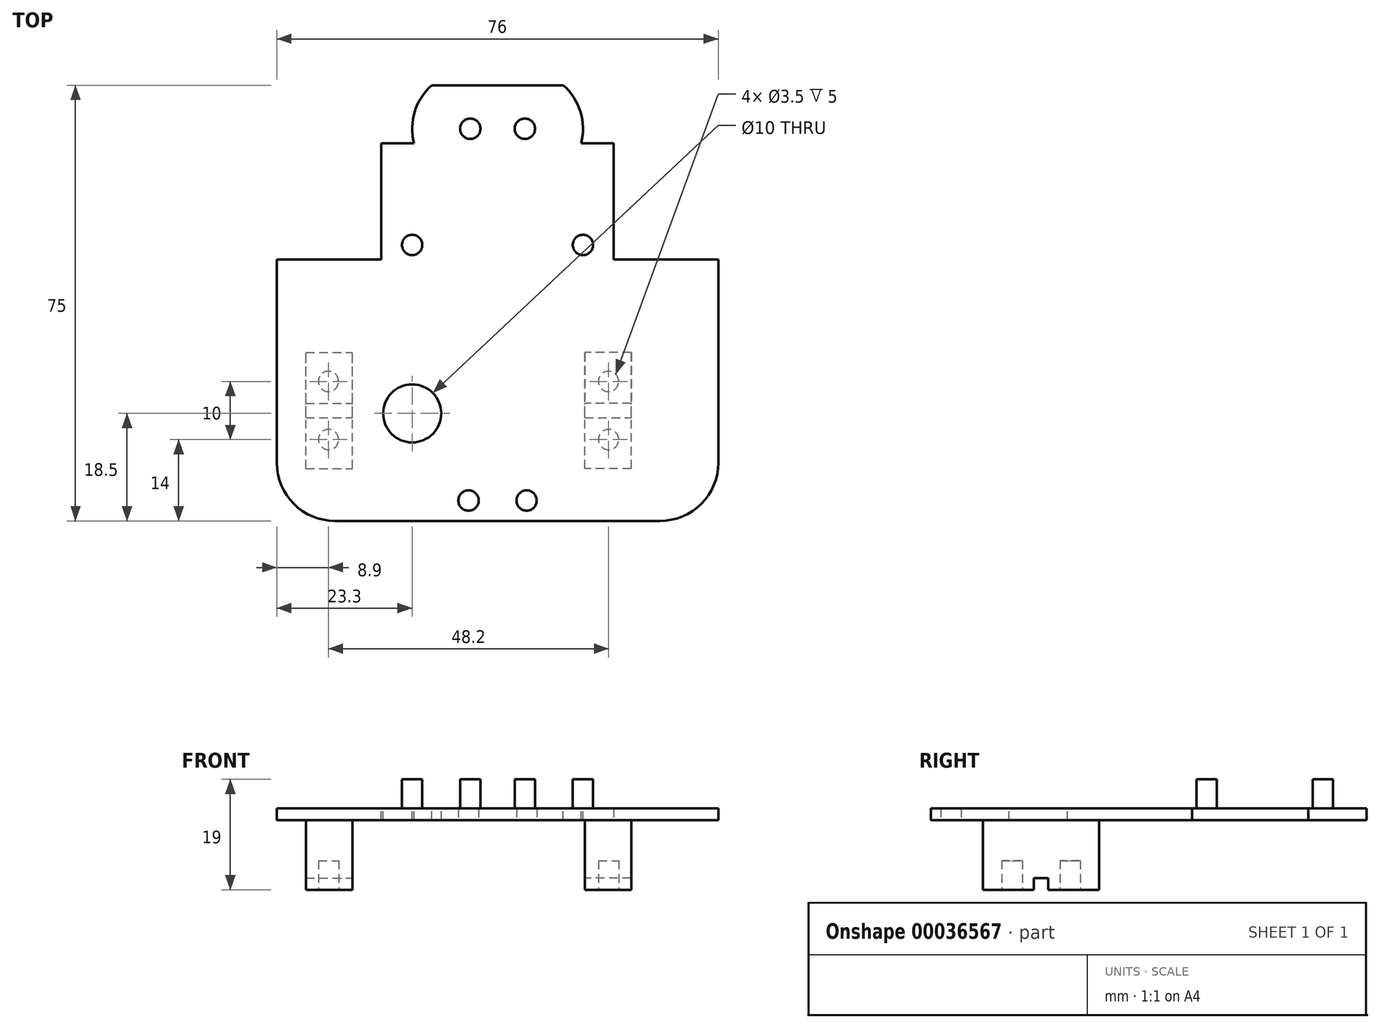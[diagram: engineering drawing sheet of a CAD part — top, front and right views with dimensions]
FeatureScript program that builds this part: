
annotation { "Feature Type Name" : "Feature", "Feature Type Description" : "" }
export const myFeature = defineFeature(function(context is Context, id is Id, definition is map)
    precondition{}
    {
        {
            var Q0;
            Q0=qCreatedBy(makeId("Top.planeOp"),FACE);
            var sketch = newSketch(context, id + "F0", { "sketchPlane" : qUnion([Q0])});
            skLineSegment(sketch, "E0.bottom", {"start": v(-20, 27.5) * mm, "end": v(20, 27.5) * mm});
            skLineSegment(sketch, "E0.top", {"start": v(-20, -2.5) * mm, "end": v(20, -2.5) * mm});
            skLineSegment(sketch, "E0.left", {"start": v(-20, 27.5) * mm, "end": v(-20, -2.5) * mm});
            skLineSegment(sketch, "E0.right", {"start": v(20, 27.5) * mm, "end": v(20, -2.5) * mm});
            skSolve(sketch);
        }
        {
            var Q0;
            Q0 = qSketchRegion(id + "F0", true);
            extrude(context, id + "F1", {"entities" : qUnion([Q0]), "depth" : 2 * mm});
        }
        {
            var Q0;
            Q0=makeQuery(id+"F1.opExtrude","CAP_FACE",FACE,{"disambiguationData":[OSD([sQuery(id+"F0.wireOp",EDGE,"E0.bottom"),sQuery(id+"F0.wireOp",EDGE,"E0.top"),sQuery(id+"F0.wireOp",EDGE,"E0.left"),sQuery(id+"F0.wireOp",EDGE,"E0.right")])],"isStart":false});
            var sketch = newSketch(context, id + "F2", { "sketchPlane" : qUnion([Q0])});
            skCircle(sketch, "E1", {"center": v(14.7, 0) * mm, "radius": 1.75 * mm});
            skCircle(sketch, "E2", {"center": v(-14.7, 0) * mm, "radius": 1.75 * mm});
            skSolve(sketch);
        }
        {
            var Q0;
            Q0=makeQuery(id+"F2.imprint","IMPRINT",FACE,{"disambiguationData":[TD([[makeQuery(id+"F2.imprint","IMPRINT",EDGE,{"derivedFrom":sQuery(id+"F2.wireOp",EDGE,"E1")}),1.0]])]});
            var Q1;
            Q1=makeQuery(id+"F2.imprint","IMPRINT",FACE,{"disambiguationData":[TD([[makeQuery(id+"F2.imprint","IMPRINT",EDGE,{"derivedFrom":sQuery(id+"F2.wireOp",EDGE,"E2")}),1.0]])]});
            extrude(context, id + "F3", {"entities" : qUnion([Q0, Q1]), "operationType" : NewBodyOperationType.ADD, "depth" : 5 * mm});
        }
        {
            var Q0;
            Q0=makeQuery(id+"F1.opExtrude","CAP_FACE",FACE,{"disambiguationData":[OSD([sQuery(id+"F0.wireOp",EDGE,"E0.bottom"),sQuery(id+"F0.wireOp",EDGE,"E0.top"),sQuery(id+"F0.wireOp",EDGE,"E0.left"),sQuery(id+"F0.wireOp",EDGE,"E0.right")])],"isStart":false});
            var sketch = newSketch(context, id + "F4", { "sketchPlane" : qUnion([Q0])});
            skCircle(sketch, "E3", {"center": v(-4.7, 20) * mm, "radius": 1.75 * mm});
            skCircle(sketch, "E4", {"center": v(4.7, 20) * mm, "radius": 1.75 * mm});
            skSolve(sketch);
        }
        {
            var Q0;
            Q0=makeQuery(id+"F4.imprint","IMPRINT",FACE,{"disambiguationData":[TD([[makeQuery(id+"F4.imprint","IMPRINT",EDGE,{"derivedFrom":sQuery(id+"F4.wireOp",EDGE,"E3")}),1.0]])]});
            var Q1;
            Q1=makeQuery(id+"F4.imprint","IMPRINT",FACE,{"disambiguationData":[TD([[makeQuery(id+"F4.imprint","IMPRINT",EDGE,{"derivedFrom":sQuery(id+"F4.wireOp",EDGE,"E4")}),1.0]])]});
            extrude(context, id + "F5", {"entities" : qUnion([Q0, Q1]), "operationType" : NewBodyOperationType.ADD, "depth" : 5 * mm});
        }
        {
            var Q0;
            Q0=makeQuery(id+"F2.imprint","IMPRINT",FACE,{"disambiguationData":[TD([[makeQuery(id+"F2.imprint","IMPRINT",EDGE,{"derivedFrom":sQuery(id+"F2.wireOp",EDGE,"E1")}),-1.0]])]});
            var sketch = newSketch(context, id + "F6", { "sketchPlane" : qUnion([Q0])});
            skArc(sketch, "E5", {"start": v(-11.3, 27.51) * mm, "mid": v(-14.26, 22.94) * mm, "end": v(-14.38, 17.5) * mm});
            skLineSegment(sketch, "E6", {"start": v(-20, 17.5) * mm, "end": v(-14.38, 17.5) * mm});
            skLineSegment(sketch, "E7", {"start": v(-20, 17.5) * mm, "end": v(-20, 27.51) * mm});
            skLineSegment(sketch, "E8", {"start": v(-20, 27.51) * mm, "end": v(-11.3, 27.51) * mm});
            skLineSegment(sketch, "E9", {"start": v(0, 31.6) * mm, "end": v(0, 7.91) * mm, "construction": true});
            skArc(sketch, "E10.MirrorCS", {"start": v(11.3, 27.51) * mm, "mid": v(14.26, 22.94) * mm, "end": v(14.38, 17.5) * mm});
            skLineSegment(sketch, "E11.MirrorCS", {"start": v(20, 27.51) * mm, "end": v(11.3, 27.51) * mm});
            skLineSegment(sketch, "E12.MirrorCS", {"start": v(20, 17.5) * mm, "end": v(20, 27.51) * mm});
            skLineSegment(sketch, "E13.MirrorCS", {"start": v(20, 17.5) * mm, "end": v(14.38, 17.5) * mm});
            skSolve(sketch);
        }
        {
            var Q0;
            Q0 = qSketchRegion(id + "F6", true);
            extrude(context, id + "F7", {"entities" : qUnion([Q0]), "operationType" : NewBodyOperationType.REMOVE, "endBound" : BoundingType.THROUGH_ALL, "oppositeDirection" : true, "depth" : 25 * mm});
        }
        {
            var Q0;
            Q0=qCreatedBy(makeId("Top.planeOp"),FACE);
            var sketch = newSketch(context, id + "F8", { "sketchPlane" : qUnion([Q0])});
            skLineSegment(sketch, "E14.bottom", {"start": v(-50, -2.5) * mm, "end": v(50, -2.5) * mm});
            skLineSegment(sketch, "E14.top", {"start": v(-50, -52.5) * mm, "end": v(50, -52.5) * mm});
            skLineSegment(sketch, "E14.left", {"start": v(-50, -2.5) * mm, "end": v(-50, -52.5) * mm});
            skLineSegment(sketch, "E14.right", {"start": v(50, -2.5) * mm, "end": v(50, -52.5) * mm});
            skSolve(sketch);
        }
        {
            var Q0;
            Q0 = qSketchRegion(id + "F8", true);
            extrude(context, id + "F9", {"entities" : qUnion([Q0]), "operationType" : NewBodyOperationType.ADD, "depth" : 2 * mm});
        }
        {
            var Q0;
            Q0=makeQuery(id+"F9.boolean.opBoolean","MERGE",FACE,{"derivedFrom":[makeQuery(id+"F1.opExtrude","CAP_FACE",FACE,{"disambiguationData":[OSD([sQuery(id+"F0.wireOp",EDGE,"E0.bottom"),sQuery(id+"F0.wireOp",EDGE,"E0.top"),sQuery(id+"F0.wireOp",EDGE,"E0.left"),sQuery(id+"F0.wireOp",EDGE,"E0.right")])],"isStart":false}),makeQuery(id+"F9.opExtrude","CAP_FACE",FACE,{"disambiguationData":[OSD([sQuery(id+"F8.wireOp",EDGE,"E14.bottom"),sQuery(id+"F8.wireOp",EDGE,"E14.top"),sQuery(id+"F8.wireOp",EDGE,"E14.left"),sQuery(id+"F8.wireOp",EDGE,"E14.right")])],"isStart":false})]});
            var sketch = newSketch(context, id + "F10", { "sketchPlane" : qUnion([Q0])});
            skCircle(sketch, "E15", {"center": v(-14.7, -29) * mm, "radius": 5 * mm});
            skSolve(sketch);
        }
        {
            var Q0;
            Q0 = qSketchRegion(id + "F10", true);
            extrude(context, id + "F11", {"entities" : qUnion([Q0]), "operationType" : NewBodyOperationType.REMOVE, "endBound" : BoundingType.THROUGH_ALL, "oppositeDirection" : true, "depth" : 25 * mm});
        }
        {
            var Q0;
            Q0=makeQuery(id+"F9.boolean.opBoolean","MERGE",FACE,{"derivedFrom":[makeQuery(id+"F1.opExtrude","CAP_FACE",FACE,{"disambiguationData":[OSD([sQuery(id+"F0.wireOp",EDGE,"E0.bottom"),sQuery(id+"F0.wireOp",EDGE,"E0.top"),sQuery(id+"F0.wireOp",EDGE,"E0.left"),sQuery(id+"F0.wireOp",EDGE,"E0.right")])],"isStart":true}),makeQuery(id+"F9.opExtrude","CAP_FACE",FACE,{"disambiguationData":[OSD([sQuery(id+"F8.wireOp",EDGE,"E14.bottom"),sQuery(id+"F8.wireOp",EDGE,"E14.top"),sQuery(id+"F8.wireOp",EDGE,"E14.left"),sQuery(id+"F8.wireOp",EDGE,"E14.right")])],"isStart":true})]});
            var sketch = newSketch(context, id + "F12", { "sketchPlane" : qUnion([Q0])});
            skLineSegment(sketch, "E16.bottom", {"start": v(-33, 38.5) * mm, "end": v(-25, 38.5) * mm});
            skLineSegment(sketch, "E16.top", {"start": v(-33, 18.5) * mm, "end": v(-25, 18.5) * mm});
            skLineSegment(sketch, "E16.left", {"start": v(-33, 38.5) * mm, "end": v(-33, 18.5) * mm});
            skLineSegment(sketch, "E16.right", {"start": v(-25, 38.5) * mm, "end": v(-25, 18.5) * mm});
            skLineSegment(sketch, "E17", {"start": v(-5, 39.4) * mm, "end": v(-5, 13.63) * mm, "construction": true});
            skLineSegment(sketch, "E18.MirrorCS", {"start": v(15, 38.5) * mm, "end": v(15, 18.5) * mm});
            skLineSegment(sketch, "E19.MirrorCS", {"start": v(23, 38.5) * mm, "end": v(15, 38.5) * mm});
            skLineSegment(sketch, "E20.MirrorCS", {"start": v(23, 38.5) * mm, "end": v(23, 18.5) * mm});
            skLineSegment(sketch, "E21.MirrorCS", {"start": v(23, 18.5) * mm, "end": v(15, 18.5) * mm});
            skSolve(sketch);
        }
        {
            var Q0;
            Q0 = qSketchRegion(id + "F12", true);
            extrude(context, id + "F13", {"entities" : qUnion([Q0]), "operationType" : NewBodyOperationType.ADD, "depth" : 10 * mm});
        }
        {
            var Q0;
            Q0=makeQuery(id+"F13.opExtrude","CAP_FACE",FACE,{"disambiguationData":[OSD([sQuery(id+"F12.wireOp",EDGE,"E16.bottom"),sQuery(id+"F12.wireOp",EDGE,"E16.top"),sQuery(id+"F12.wireOp",EDGE,"E16.left"),sQuery(id+"F12.wireOp",EDGE,"E16.right")])],"isStart":false});
            var sketch = newSketch(context, id + "F14", { "sketchPlane" : qUnion([Q0])});
            skLineSegment(sketch, "E22.bottom", {"start": v(-33, 18.5) * mm, "end": v(-25, 18.5) * mm});
            skLineSegment(sketch, "E22.top", {"start": v(-33, 27.25) * mm, "end": v(-25, 27.25) * mm});
            skLineSegment(sketch, "E22.left", {"start": v(-33, 18.5) * mm, "end": v(-33, 27.25) * mm});
            skLineSegment(sketch, "E22.right", {"start": v(-25, 18.5) * mm, "end": v(-25, 27.25) * mm});
            skLineSegment(sketch, "E23.bottom", {"start": v(-33, 38.5) * mm, "end": v(-25, 38.5) * mm});
            skLineSegment(sketch, "E23.top", {"start": v(-33, 29.75) * mm, "end": v(-25, 29.75) * mm});
            skLineSegment(sketch, "E23.left", {"start": v(-33, 38.5) * mm, "end": v(-33, 29.75) * mm});
            skLineSegment(sketch, "E23.right", {"start": v(-25, 38.5) * mm, "end": v(-25, 29.75) * mm});
            skLineSegment(sketch, "E24.bottom", {"start": v(15, 38.5) * mm, "end": v(23, 38.5) * mm});
            skLineSegment(sketch, "E24.top", {"start": v(15, 29.75) * mm, "end": v(23, 29.75) * mm});
            skLineSegment(sketch, "E24.left", {"start": v(15, 38.5) * mm, "end": v(15, 29.75) * mm});
            skLineSegment(sketch, "E24.right", {"start": v(23, 38.5) * mm, "end": v(23, 29.75) * mm});
            skLineSegment(sketch, "E25.bottom", {"start": v(23, 18.5) * mm, "end": v(15, 18.5) * mm});
            skLineSegment(sketch, "E25.top", {"start": v(23, 27.25) * mm, "end": v(15, 27.25) * mm});
            skLineSegment(sketch, "E25.left", {"start": v(23, 18.5) * mm, "end": v(23, 27.25) * mm});
            skLineSegment(sketch, "E25.right", {"start": v(15, 18.5) * mm, "end": v(15, 27.25) * mm});
            skSolve(sketch);
        }
        {
            var Q0;
            Q0 = qSketchRegion(id + "F14", true);
            extrude(context, id + "F15", {"entities" : qUnion([Q0]), "operationType" : NewBodyOperationType.ADD, "depth" : 2 * mm});
        }
        {
            var Q0;
            Q0=makeQuery(id+"F15.opExtrude","CAP_FACE",FACE,{"disambiguationData":[OSD([sQuery(id+"F14.wireOp",EDGE,"E23.bottom"),sQuery(id+"F14.wireOp",EDGE,"E23.top"),sQuery(id+"F14.wireOp",EDGE,"E23.left"),sQuery(id+"F14.wireOp",EDGE,"E23.right")])],"isStart":false});
            var sketch = newSketch(context, id + "F16", { "sketchPlane" : qUnion([Q0])});
            skCircle(sketch, "E26", {"center": v(-29.1, 33.5) * mm, "radius": 1.75 * mm});
            skCircle(sketch, "E27", {"center": v(-29.1, 23.5) * mm, "radius": 1.75 * mm});
            skLineSegment(sketch, "E28", {"start": v(-5, 37.97) * mm, "end": v(-5, 22.56) * mm, "construction": true});
            skLineSegment(sketch, "E29", {"start": v(-34.59, 28.5) * mm, "end": v(-23.06, 28.5) * mm, "construction": true});
            skCircle(sketch, "E30.MirrorC", {"center": v(19.1, 23.5) * mm, "radius": 1.75 * mm});
            skCircle(sketch, "E31.MirrorC", {"center": v(19.1, 33.5) * mm, "radius": 1.75 * mm});
            skSolve(sketch);
        }
        {
            var Q0;
            Q0 = qSketchRegion(id + "F16", true);
            extrude(context, id + "F17", {"entities" : qUnion([Q0]), "operationType" : NewBodyOperationType.REMOVE, "oppositeDirection" : true, "depth" : 5 * mm});
        }
        {
            var Q0;
            Q0=makeQuery(id+"F9.boolean.opBoolean","MERGE",FACE,{"derivedFrom":[makeQuery(id+"F1.opExtrude","CAP_FACE",FACE,{"disambiguationData":[OSD([sQuery(id+"F0.wireOp",EDGE,"E0.bottom"),sQuery(id+"F0.wireOp",EDGE,"E0.top"),sQuery(id+"F0.wireOp",EDGE,"E0.left"),sQuery(id+"F0.wireOp",EDGE,"E0.right")])],"isStart":true}),makeQuery(id+"F9.opExtrude","CAP_FACE",FACE,{"disambiguationData":[OSD([sQuery(id+"F8.wireOp",EDGE,"E14.bottom"),sQuery(id+"F8.wireOp",EDGE,"E14.top"),sQuery(id+"F8.wireOp",EDGE,"E14.left"),sQuery(id+"F8.wireOp",EDGE,"E14.right")])],"isStart":true})]});
            var sketch = newSketch(context, id + "F18", { "sketchPlane" : qUnion([Q0])});
            skLineSegment(sketch, "E32.bottom", {"start": v(-50, 52.5) * mm, "end": v(50, 52.5) * mm});
            skLineSegment(sketch, "E32.top", {"start": v(-38, 47.5) * mm, "end": v(38, 47.5) * mm});
            skLineSegment(sketch, "E32.left", {"start": v(-50, 52.5) * mm, "end": v(-50, 47.5) * mm});
            skLineSegment(sketch, "E32.right", {"start": v(50, 52.5) * mm, "end": v(50, 47.5) * mm});
            skLineSegment(sketch, "E33.bottom", {"start": v(-50, 52.5) * mm, "end": v(-38, 52.5) * mm});
            skLineSegment(sketch, "E33.top", {"start": v(-50, 2.5) * mm, "end": v(-38, 2.5) * mm});
            skLineSegment(sketch, "E33.left", {"start": v(-50, 52.5) * mm, "end": v(-50, 2.5) * mm});
            skLineSegment(sketch, "E33.right", {"start": v(-38, 47.5) * mm, "end": v(-38, 2.5) * mm});
            skLineSegment(sketch, "E34.bottom", {"start": v(50, 52.5) * mm, "end": v(38, 52.5) * mm});
            skLineSegment(sketch, "E34.top", {"start": v(50, 2.5) * mm, "end": v(38, 2.5) * mm});
            skLineSegment(sketch, "E34.left", {"start": v(50, 52.5) * mm, "end": v(50, 2.5) * mm});
            skLineSegment(sketch, "E34.right", {"start": v(38, 47.5) * mm, "end": v(38, 2.5) * mm});
            skLineSegment(sketch, "E35", {"start": v(0, -32.2) * mm, "end": v(0, 56.92) * mm, "construction": true});
            skPoint(sketch, "E35.endSnap0", {"position": v(0, 52.5) * mm});
            skCircle(sketch, "E36", {"center": v(-5, 44) * mm, "radius": 1.75 * mm});
            skCircle(sketch, "E37.MirrorC", {"center": v(5, 44) * mm, "radius": 1.75 * mm});
            skSolve(sketch);
        }
        {
            var Q0;
            Q0 = qSketchRegion(id + "F18", true);
            extrude(context, id + "F19", {"entities" : qUnion([Q0]), "operationType" : NewBodyOperationType.REMOVE, "endBound" : BoundingType.THROUGH_ALL, "oppositeDirection" : true, "depth" : 25 * mm});
        }
        {
            var Q0;
            Q0=makeQuery(id+"F19.boolean.opBoolean","COPY",EDGE,{"derivedFrom":makeQuery(id+"F19.opExtrude","SWEPT_EDGE",EDGE,{"disambiguationData":[OSD([sQuery(id+"F8.wireOp",EDGE,"E14.bottom"),sQuery(id+"F18.wireOp",EDGE,"E33.top"),sQuery(id+"F18.wireOp",EDGE,"E33.right")])]})});
            var Q1;
            Q1=makeQuery(id+"F19.boolean.opBoolean","COPY",EDGE,{"derivedFrom":makeQuery(id+"F19.opExtrude","SWEPT_EDGE",EDGE,{"disambiguationData":[OSD([sQuery(id+"F8.wireOp",EDGE,"E14.bottom"),sQuery(id+"F18.wireOp",EDGE,"E34.top"),sQuery(id+"F18.wireOp",EDGE,"E34.right")])]})});
            var Q2;
            Q2=makeQuery(id+"F19.boolean.opBoolean","COPY",EDGE,{"derivedFrom":makeQuery(id+"F19.opExtrude","SWEPT_EDGE",EDGE,{"disambiguationData":[OSD([sQuery(id+"F18.wireOp",EDGE,"E32.top"),sQuery(id+"F18.wireOp",EDGE,"E33.right")])]})});
            var Q3;
            Q3=makeQuery(id+"F19.boolean.opBoolean","COPY",EDGE,{"derivedFrom":makeQuery(id+"F19.opExtrude","SWEPT_EDGE",EDGE,{"disambiguationData":[OSD([sQuery(id+"F18.wireOp",EDGE,"E32.top"),sQuery(id+"F18.wireOp",EDGE,"E34.right")])]})});
            fillet(context, id + "F20", {"entities" : qUnion([Q0, Q1, Q2, Q3]), "radius" : 10 * mm, "tangentPropagation" : true, "allowEdgeOverflow" : false});
        }
    });
